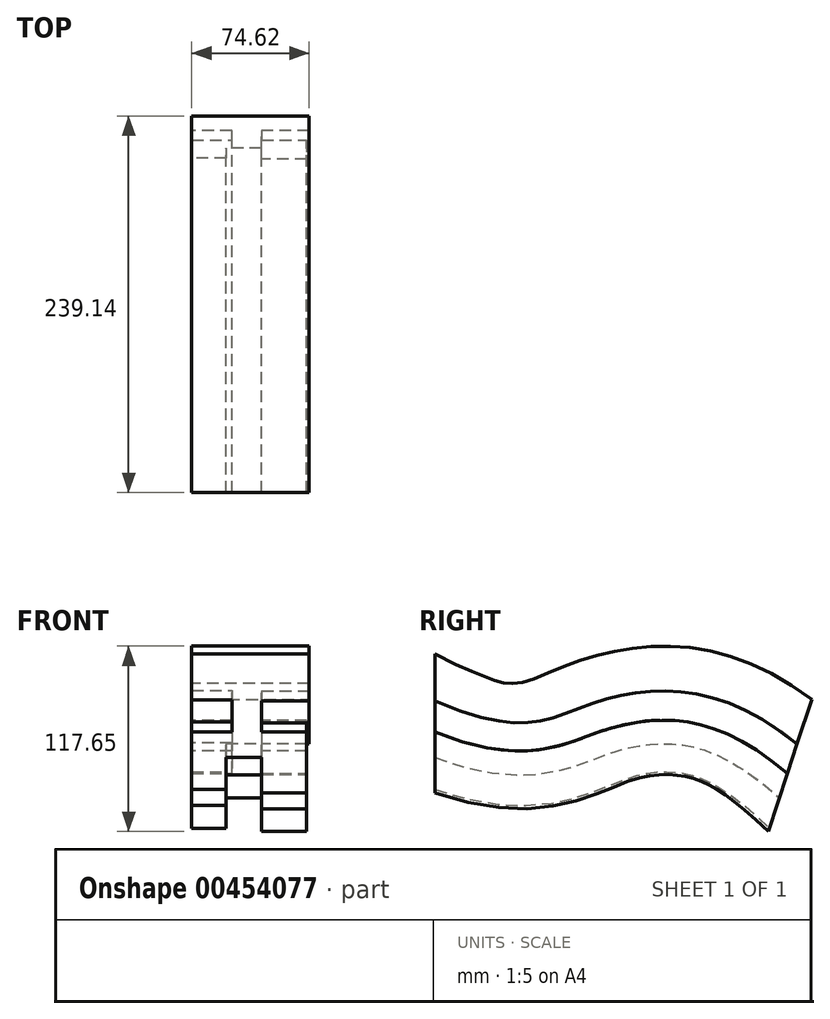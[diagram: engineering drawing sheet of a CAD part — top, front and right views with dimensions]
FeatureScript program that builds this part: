
annotation { "Feature Type Name" : "Feature", "Feature Type Description" : "" }
export const myFeature = defineFeature(function(context is Context, id is Id, definition is map)
    precondition{}
    {
        {
            var Q0;
            Q0=qCreatedBy(makeId("Front.planeOp"),FACE);
            var sketch = newSketch(context, id + "F0", { "sketchPlane" : qUnion([Q0])});
            skLineSegment(sketch, "E0", {"start": v(-33.57, 49.45) * mm, "end": v(41.05, 49.45) * mm});
            skLineSegment(sketch, "E1", {"start": v(41.05, 49.45) * mm, "end": v(41.05, 19.7) * mm});
            skLineSegment(sketch, "E2", {"start": v(41.05, 19.7) * mm, "end": v(10.78, 19.7) * mm});
            skLineSegment(sketch, "E3", {"start": v(10.78, 19.7) * mm, "end": v(10.78, 0) * mm});
            skLineSegment(sketch, "E4", {"start": v(10.78, 0) * mm, "end": v(39.48, 0) * mm});
            skLineSegment(sketch, "E5", {"start": v(39.48, 0) * mm, "end": v(39.48, -38.73) * mm});
            skLineSegment(sketch, "E6", {"start": v(39.48, -38.73) * mm, "end": v(10.78, -38.73) * mm});
            skLineSegment(sketch, "E7", {"start": v(10.78, -38.73) * mm, "end": v(10.78, -16.3) * mm});
            skLineSegment(sketch, "E8", {"start": v(10.78, -16.3) * mm, "end": v(-11.66, -16.3) * mm});
            skLineSegment(sketch, "E9", {"start": v(-11.66, -16.3) * mm, "end": v(-11.66, -36.65) * mm});
            skLineSegment(sketch, "E10", {"start": v(-11.66, -36.65) * mm, "end": v(-33.57, -36.65) * mm});
            skLineSegment(sketch, "E11", {"start": v(-33.57, -36.65) * mm, "end": v(-33.57, 0) * mm});
            skLineSegment(sketch, "E12", {"start": v(-33.57, 0) * mm, "end": v(-8, 0) * mm});
            skLineSegment(sketch, "E13", {"start": v(-8, 0) * mm, "end": v(-8, 20.23) * mm});
            skLineSegment(sketch, "E14", {"start": v(-8, 20.23) * mm, "end": v(-33.57, 20.23) * mm});
            skLineSegment(sketch, "E15", {"start": v(-33.57, 20.23) * mm, "end": v(-33.57, 49.45) * mm});
            skSolve(sketch);
        }
        {
            var Q0;
            Q0=qCreatedBy(makeId("Right.planeOp"),FACE);
            var sketch = newSketch(context, id + "F1", { "sketchPlane" : qUnion([Q0])});
            skFitSpline(sketch, "E16", {"points": [v(0, 0) * mm, v(104.07, 0) * mm, v(154.46, 7.02) * mm, v(223.79, -26.33) * mm], "startDerivative": vector(428.1, -173.21) * mm, "endDerivative": vector(238.82, -201.2) * mm});
            skSolve(sketch);
        }
        {
            var Q0;
            Q0=makeQuery(id+"F0.imprint","IMPRINT",FACE,{"disambiguationData":[TD([[makeQuery(id+"F0.imprint","IMPRINT",EDGE,{"derivedFrom":sQuery(id+"F0.wireOp",EDGE,"E0")}),-1.0]])]});
            var Q1;
            Q1=sQuery(id+"F1.wireOp",EDGE,"E16");
            sweep(context, id + "F2", {"profiles" : qUnion([Q0]), "path" : qUnion([Q1])});
        }
    });
